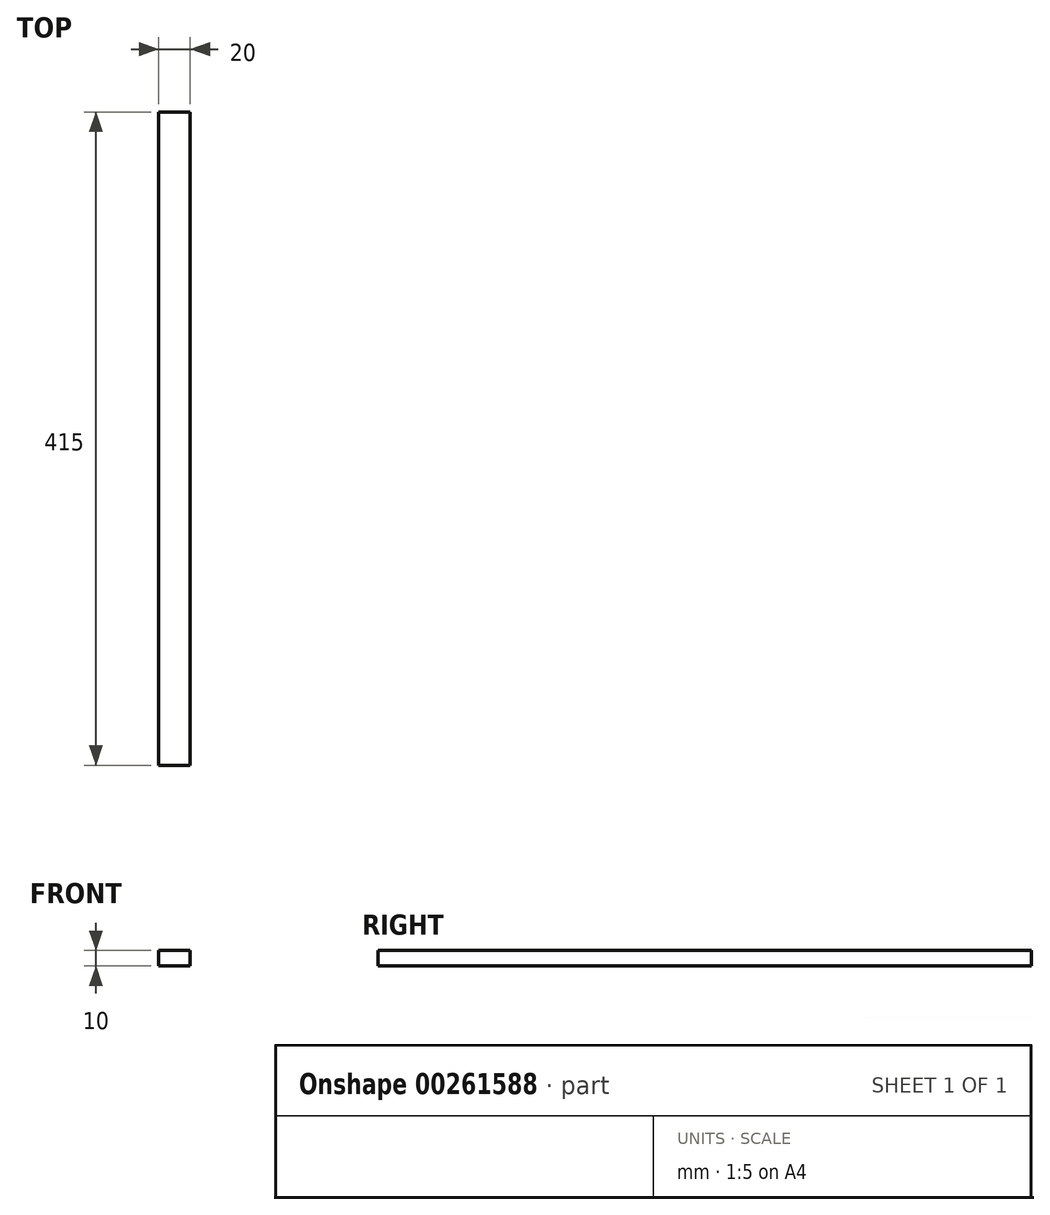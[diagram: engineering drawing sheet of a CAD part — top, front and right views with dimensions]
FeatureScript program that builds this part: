
annotation { "Feature Type Name" : "Feature", "Feature Type Description" : "" }
export const myFeature = defineFeature(function(context is Context, id is Id, definition is map)
    precondition{}
    {
        {
            var Q0;
            Q0=qCreatedBy(makeId("Front.planeOp"),FACE);
            var sketch = newSketch(context, id + "F0", { "sketchPlane" : qUnion([Q0])});
            skLineSegment(sketch, "E0.bottom", {"start": v(0, 0) * mm, "end": v(20, 0) * mm});
            skLineSegment(sketch, "E0.top", {"start": v(0, -10) * mm, "end": v(20, -10) * mm});
            skLineSegment(sketch, "E0.left", {"start": v(0, 0) * mm, "end": v(0, -10) * mm});
            skLineSegment(sketch, "E0.right", {"start": v(20, 0) * mm, "end": v(20, -10) * mm});
            skSolve(sketch);
        }
        {
            var Q0;
            Q0 = qSketchRegion(id + "F0", true);
            extrude(context, id + "F1", {"entities" : qUnion([Q0]), "depth" : 415 * mm});
        }
    });
